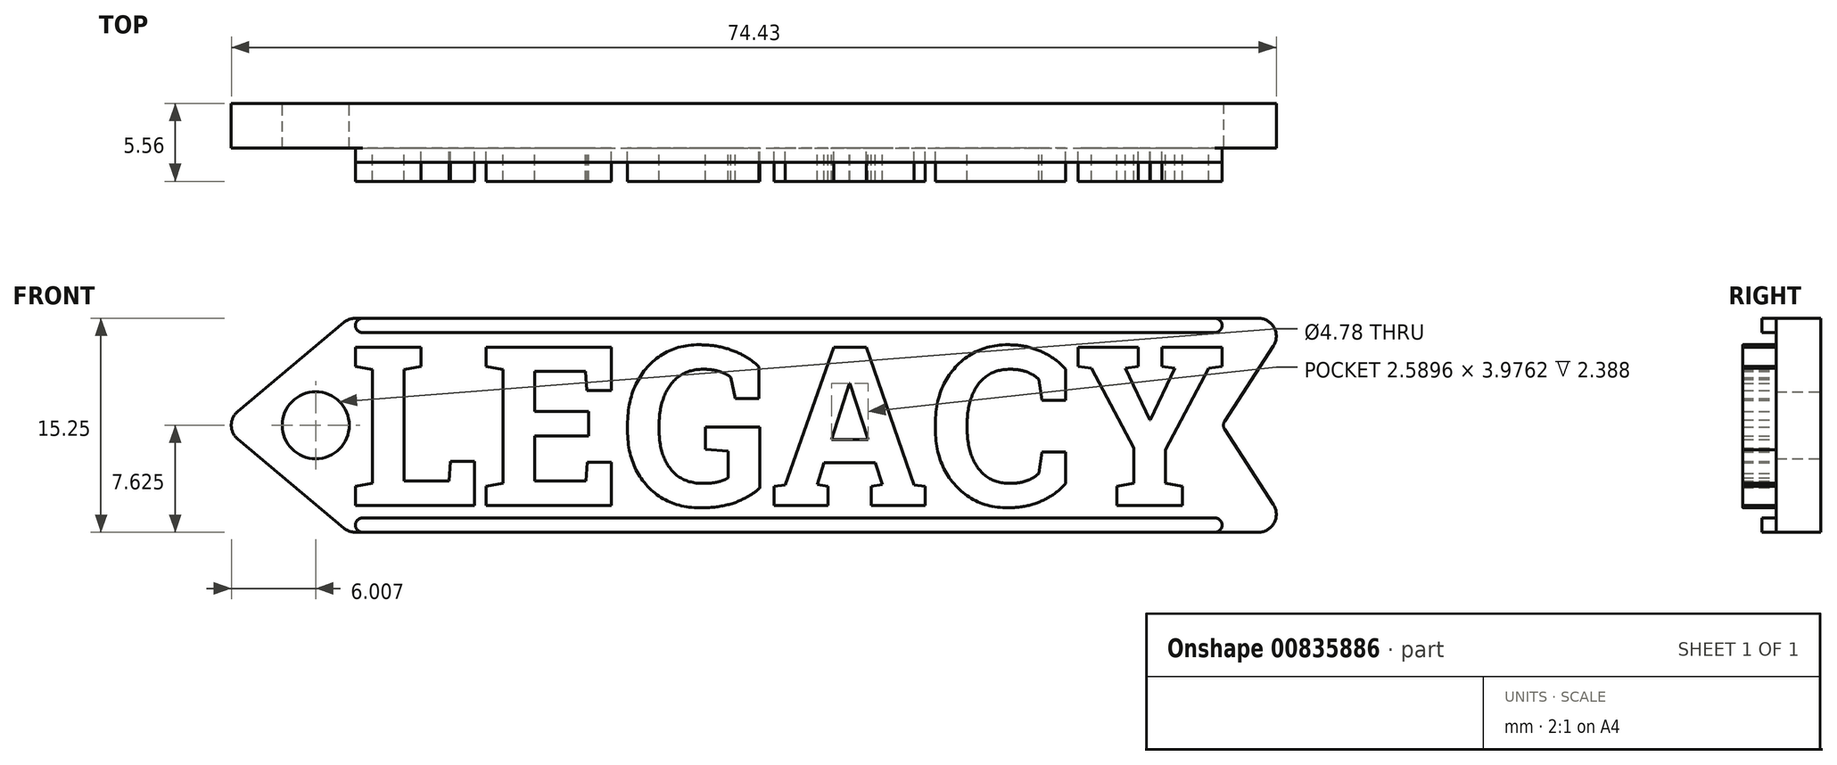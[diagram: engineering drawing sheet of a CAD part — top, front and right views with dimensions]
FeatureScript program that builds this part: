
annotation { "Feature Type Name" : "Feature", "Feature Type Description" : "" }
export const myFeature = defineFeature(function(context is Context, id is Id, definition is map)
    precondition{}
    {
        {
            var Q0;
            Q0=qCreatedBy(makeId("Front.planeOp"),FACE);
            var sketch = newSketch(context, id + "F0", { "sketchPlane" : qUnion([Q0])});
            skLineSegment(sketch, "E0.bottom", {"start": v(0, 0) * mm, "end": v(76.2, 0) * mm});
            skLineSegment(sketch, "E0.top", {"start": v(0, 19.05) * mm, "end": v(76.2, 19.05) * mm});
            skLineSegment(sketch, "E0.left", {"start": v(0, 0) * mm, "end": v(0, 19.05) * mm});
            skLineSegment(sketch, "E0.right", {"start": v(76.2, 0) * mm, "end": v(76.2, 19.05) * mm});
            skLineSegment(sketch, "E1", {"start": v(0, 9.53) * mm, "end": v(11.35, 19.05) * mm});
            skLineSegment(sketch, "E2", {"start": v(0, 9.53) * mm, "end": v(11.35, 0) * mm});
            skLineSegment(sketch, "E3", {"start": v(0, 9.53) * mm, "end": v(11.35, 9.53) * mm});
            skCircle(sketch, "E4", {"center": v(6.72, 9.53) * mm, "radius": 2.39 * mm});
            skText(sketch, "E5", { "text": "LEGACY", "fontName": "RobotoSlab-Bold.ttf"});
            skLineSegment(sketch, "E6", {"start": v(76.2, 19.05) * mm, "end": v(76.2, 15.24) * mm});
            skLineSegment(sketch, "E7", {"start": v(76.2, 0) * mm, "end": v(76.2, 3.81) * mm});
            skLineSegment(sketch, "E8", {"start": v(76.2, 1.9) * mm, "end": v(9.08, 1.9) * mm});
            skLineSegment(sketch, "E9", {"start": v(76.2, 17.15) * mm, "end": v(9.08, 17.15) * mm});
            const initialGuessF0  = {"E5": [0.01135, 0.00381, 1, 0, 0.01143]};
            skSetInitialGuess(sketch, initialGuessF0);
            skSolve(sketch);
        }
        {
            var Q0;
            {var subQ1=sQuery(id+"F0.wireOp",EDGE,"E0.right");Q0=makeQuery(id+"F0.imprint","IMPRINT",FACE,{"disambiguationData":[TD([[makeQuery(id+"F0.imprint","IMPRINT",EDGE,{"derivedFrom":subQ1}),1.0]])]});}
            var Q1;
            {var subQ0=sQuery(id+"F0.wireOp",EDGE,"E0.right");Q1=makeQuery(id+"F0.imprint","IMPRINT",FACE,{"disambiguationData":[TD([[makeQuery(id+"F0.imprint","IMPRINT",EDGE,{"derivedFrom":subQ0}),1.0]])]});}
            var Q2;
            Q2=makeQuery(id+"F0.imprint","IMPRINT",FACE,{"disambiguationData":[TD([[makeQuery(id+"F0.imprint","IMPRINT",EDGE,{"derivedFrom":sQuery(id+"F0.wireOp",EDGE,"E5.sketch_text.stroke-0")}),-1.0]])]});
            var Q3;
            Q3=makeQuery(id+"F0.imprint","IMPRINT",FACE,{"disambiguationData":[TD([[makeQuery(id+"F0.imprint","IMPRINT",EDGE,{"derivedFrom":sQuery(id+"F0.wireOp",EDGE,"E5.sketch_text.stroke-16")}),-1.0]])]});
            var Q4;
            Q4=makeQuery(id+"F0.imprint","IMPRINT",FACE,{"disambiguationData":[TD([[makeQuery(id+"F0.imprint","IMPRINT",EDGE,{"derivedFrom":sQuery(id+"F0.wireOp",EDGE,"E5.sketch_text.stroke-37")}),-1.0]])]});
            var Q5;
            Q5=makeQuery(id+"F0.imprint","IMPRINT",FACE,{"disambiguationData":[TD([[makeQuery(id+"F0.imprint","IMPRINT",EDGE,{"derivedFrom":sQuery(id+"F0.wireOp",EDGE,"E5.sketch_text.stroke-63")}),-1.0]])]});
            var Q6;
            Q6=makeQuery(id+"F0.imprint","IMPRINT",FACE,{"disambiguationData":[TD([[makeQuery(id+"F0.imprint","IMPRINT",EDGE,{"derivedFrom":sQuery(id+"F0.wireOp",EDGE,"E5.sketch_text.stroke-79")}),1.0]])]});
            var Q7;
            Q7=makeQuery(id+"F0.imprint","IMPRINT",FACE,{"disambiguationData":[TD([[makeQuery(id+"F0.imprint","IMPRINT",EDGE,{"derivedFrom":sQuery(id+"F0.wireOp",EDGE,"E5.sketch_text.stroke-83")}),-1.0]])]});
            var Q8;
            Q8=makeQuery(id+"F0.imprint","IMPRINT",FACE,{"disambiguationData":[TD([[makeQuery(id+"F0.imprint","IMPRINT",EDGE,{"derivedFrom":sQuery(id+"F0.wireOp",EDGE,"E5.sketch_text.stroke-107")}),-1.0]])]});
            extrude(context, id + "F1", {"entities" : qUnion([Q0, Q1, Q2, Q3, Q4, Q5, Q6, Q7, Q8]), "depth" : 3.17 * mm, "offsetDistance" : 25.4 * mm});
        }
        {
            var Q0;
            Q0=makeQuery(id+"F1.opExtrude","CAP_FACE",FACE,{"disambiguationData":[OSD([sQuery(id+"F0.wireOp",EDGE,"E0.right"),sQuery(id+"F0.wireOp",EDGE,"E1"),sQuery(id+"F0.wireOp",EDGE,"E2"),sQuery(id+"F0.wireOp",EDGE,"E6"),sQuery(id+"F0.wireOp",EDGE,"E7"),sQuery(id+"F0.wireOp",EDGE,"E8"),sQuery(id+"F0.wireOp",EDGE,"E9")])],"isStart":false});
            var sketch = newSketch(context, id + "F2", { "sketchPlane" : qUnion([Q0])});
            skLineSegment(sketch, "E10.bottom", {"start": v(0, 0) * mm, "end": v(76.2, 0) * mm});
            skLineSegment(sketch, "E10.top", {"start": v(0, 19.05) * mm, "end": v(76.2, 19.05) * mm});
            skLineSegment(sketch, "E10.left", {"start": v(0, 0) * mm, "end": v(0, 19.05) * mm});
            skLineSegment(sketch, "E10.right", {"start": v(76.2, 0) * mm, "end": v(76.2, 19.05) * mm});
            skText(sketch, "E11", { "text": "LEGACY", "fontName": "RobotoSlab-Bold.ttf"});
            skLineSegment(sketch, "E12", {"start": v(0, 9.53) * mm, "end": v(11.35, 19.05) * mm});
            skLineSegment(sketch, "E13", {"start": v(0, 9.53) * mm, "end": v(11.35, 0) * mm});
            const initialGuessF2  = {"E11": [0.00912, 0.00381, 1, 0, 0.01143]};
            skSetInitialGuess(sketch, initialGuessF2);
            skSolve(sketch);
        }
        {
            var Q0;
            Q0=makeQuery(id+"F2.imprint","IMPRINT",FACE,{"disambiguationData":[TD([[makeQuery(id+"F2.imprint","IMPRINT",EDGE,{"derivedFrom":sQuery(id+"F2.wireOp",EDGE,"E11.sketch_text.stroke-0")}),-1.0]])]});
            var Q1;
            Q1=makeQuery(id+"F2.imprint","IMPRINT",FACE,{"disambiguationData":[TD([[makeQuery(id+"F2.imprint","IMPRINT",EDGE,{"derivedFrom":sQuery(id+"F2.wireOp",EDGE,"E11.sketch_text.stroke-16")}),-1.0]])]});
            var Q2;
            Q2=makeQuery(id+"F2.imprint","IMPRINT",FACE,{"disambiguationData":[TD([[makeQuery(id+"F2.imprint","IMPRINT",EDGE,{"derivedFrom":sQuery(id+"F2.wireOp",EDGE,"E11.sketch_text.stroke-37")}),-1.0]])]});
            var Q3;
            Q3=makeQuery(id+"F2.imprint","IMPRINT",FACE,{"disambiguationData":[TD([[makeQuery(id+"F2.imprint","IMPRINT",EDGE,{"derivedFrom":sQuery(id+"F2.wireOp",EDGE,"E11.sketch_text.stroke-63")}),-1.0]])]});
            var Q4;
            Q4=makeQuery(id+"F2.imprint","IMPRINT",FACE,{"disambiguationData":[TD([[makeQuery(id+"F2.imprint","IMPRINT",EDGE,{"derivedFrom":sQuery(id+"F2.wireOp",EDGE,"E11.sketch_text.stroke-83")}),-1.0]])]});
            var Q5;
            Q5=makeQuery(id+"F2.imprint","IMPRINT",FACE,{"disambiguationData":[TD([[makeQuery(id+"F2.imprint","IMPRINT",EDGE,{"derivedFrom":sQuery(id+"F2.wireOp",EDGE,"E11.sketch_text.stroke-107")}),-1.0]])]});
            extrude(context, id + "F3", {"entities" : qUnion([Q0, Q1, Q2, Q3, Q4, Q5]), "operationType" : NewBodyOperationType.ADD, "depth" : 2.4 * mm, "offsetDistance" : 25.4 * mm});
        }
        {
            var Q0;
            {var subQ0=sQuery(id+"F0.wireOp",EDGE,"E7");var subQ1=sQuery(id+"F0.wireOp",EDGE,"E6");var subQ2=sQuery(id+"F0.wireOp",EDGE,"E0.right");var subQ3=sQuery(id+"F0.wireOp",EDGE,"E2");var subQ4=sQuery(id+"F0.wireOp",EDGE,"E4");var subQ5=sQuery(id+"F0.wireOp",EDGE,"E8");var subQ6=sQuery(id+"F0.wireOp",EDGE,"E9");var subQ7=sQuery(id+"F0.wireOp",EDGE,"E1");Q0=makeQuery(id+"F3.boolean.opBoolean","SPLIT",FACE,{"disambiguationData":[TD([makeQuery(id+"F1.opExtrude","SWEPT_FACE",FACE,{"disambiguationData":[OSD([subQ4])]})])],"derivedFrom":makeQuery(id+"F1.opExtrude","CAP_FACE",FACE,{"disambiguationData":[OSD([subQ4,subQ2,subQ7,subQ3,subQ1,subQ0,subQ5,subQ6])],"isStart":false})});}
            var sketch = newSketch(context, id + "F4", { "sketchPlane" : qUnion([Q0])});
            skLineSegment(sketch, "E14", {"start": v(71.27, 9.53) * mm, "end": v(76.2, 17.15) * mm});
            skLineSegment(sketch, "E15", {"start": v(71.27, 9.53) * mm, "end": v(76.2, 1.9) * mm});
            skSolve(sketch);
        }
        {
            var Q0;
            Q0=makeQuery(id+"F4.imprint","IMPRINT",FACE,{"disambiguationData":[TD([[makeQuery(id+"F4.imprint","IMPRINT",EDGE,{"derivedFrom":sQuery(id+"F4.wireOp",EDGE,"E14")}),-1.0]])]});
            extrude(context, id + "F5", {"entities" : qUnion([Q0]), "operationType" : NewBodyOperationType.REMOVE, "oppositeDirection" : true, "depth" : 25.4 * mm, "offsetDistance" : 25.4 * mm});
        }
        {
            var Q0;
            Q0=makeQuery(id+"F1.opExtrude","SWEPT_EDGE",EDGE,{"disambiguationData":[OSD([sQuery(id+"F0.wireOp",EDGE,"E0.left"),sQuery(id+"F0.wireOp",EDGE,"E1"),sQuery(id+"F0.wireOp",EDGE,"E2")])]});
            var Q1;
            Q1=makeQuery(id+"F1.opExtrude","SWEPT_EDGE",EDGE,{"disambiguationData":[OSD([sQuery(id+"F0.wireOp",EDGE,"E1"),sQuery(id+"F0.wireOp",EDGE,"E9")])]});
            var Q2;
            Q2=makeQuery(id+"F1.opExtrude","SWEPT_EDGE",EDGE,{"disambiguationData":[OSD([sQuery(id+"F0.wireOp",EDGE,"E2"),sQuery(id+"F0.wireOp",EDGE,"E8")])]});
            fillet(context, id + "F6", {"entities" : qUnion([Q0, Q1, Q2]), "radius" : 1.27 * mm, "tangentPropagation" : true, "allowEdgeOverflow" : false});
        }
        {
            var Q0;
            {var subQ0=sQuery(id+"F0.wireOp",EDGE,"E9");var subQ1=sQuery(id+"F0.wireOp",EDGE,"E6");Q0=makeQuery(id+"F5.boolean.opBoolean","MERGE",EDGE,{"derivedFrom":[makeQuery(id+"F1.opExtrude","SWEPT_EDGE",EDGE,{"disambiguationData":[OSD([subQ1,subQ0])]}),makeQuery(id+"F5.opExtrude","SWEPT_EDGE",EDGE,{"disambiguationData":[OSD([sQuery(id+"F0.wireOp",EDGE,"E0.right"),subQ1,sQuery(id+"F0.wireOp",EDGE,"E7"),subQ0,sQuery(id+"F4.wireOp",EDGE,"E14")])]})]});}
            var Q1;
            {var subQ0=sQuery(id+"F0.wireOp",EDGE,"E8");var subQ1=sQuery(id+"F0.wireOp",EDGE,"E7");Q1=makeQuery(id+"F5.boolean.opBoolean","MERGE",EDGE,{"derivedFrom":[makeQuery(id+"F1.opExtrude","SWEPT_EDGE",EDGE,{"disambiguationData":[OSD([subQ1,subQ0])]}),makeQuery(id+"F5.opExtrude","SWEPT_EDGE",EDGE,{"disambiguationData":[OSD([sQuery(id+"F0.wireOp",EDGE,"E0.right"),sQuery(id+"F0.wireOp",EDGE,"E6"),subQ1,subQ0,sQuery(id+"F4.wireOp",EDGE,"E15")])]})]});}
            var Q2;
            Q2=makeQuery(id+"F5.boolean.opBoolean","COPY",EDGE,{"derivedFrom":makeQuery(id+"F5.opExtrude","SWEPT_EDGE",EDGE,{"disambiguationData":[OSD([sQuery(id+"F4.wireOp",EDGE,"E14"),sQuery(id+"F4.wireOp",EDGE,"E15")])]})});
            fillet(context, id + "F7", {"entities" : qUnion([Q0, Q1, Q2]), "radius" : 0.5 * mm, "tangentPropagation" : true, "allowEdgeOverflow" : false});
        }
        {
            var Q0;
            {var subQ0=sQuery(id+"F0.wireOp",EDGE,"E7");var subQ1=sQuery(id+"F0.wireOp",EDGE,"E6");var subQ2=sQuery(id+"F0.wireOp",EDGE,"E0.right");var subQ3=sQuery(id+"F0.wireOp",EDGE,"E2");var subQ4=sQuery(id+"F0.wireOp",EDGE,"E4");var subQ5=sQuery(id+"F0.wireOp",EDGE,"E8");var subQ6=sQuery(id+"F0.wireOp",EDGE,"E9");var subQ7=sQuery(id+"F0.wireOp",EDGE,"E1");Q0=makeQuery(id+"F3.boolean.opBoolean","SPLIT",FACE,{"disambiguationData":[TD([makeQuery(id+"F1.opExtrude","SWEPT_FACE",FACE,{"disambiguationData":[OSD([subQ4])]})])],"derivedFrom":makeQuery(id+"F1.opExtrude","CAP_FACE",FACE,{"disambiguationData":[OSD([subQ4,subQ2,subQ7,subQ3,subQ1,subQ0,subQ5,subQ6])],"isStart":false})});}
            var sketch = newSketch(context, id + "F8", { "sketchPlane" : qUnion([Q0])});
            skLineSegment(sketch, "E16", {"start": v(9.54, 17.15) * mm, "end": v(9.54, 16.13) * mm});
            skLineSegment(sketch, "E17", {"start": v(9.54, 1.9) * mm, "end": v(9.54, 2.92) * mm});
            skLineSegment(sketch, "E18", {"start": v(9.54, 16.13) * mm, "end": v(71.27, 16.13) * mm});
            skLineSegment(sketch, "E19", {"start": v(71.27, 16.13) * mm, "end": v(71.27, 17.15) * mm});
            skLineSegment(sketch, "E20", {"start": v(9.54, 2.92) * mm, "end": v(71.27, 2.92) * mm});
            skLineSegment(sketch, "E21", {"start": v(71.27, 2.92) * mm, "end": v(71.27, 1.9) * mm});
            skSolve(sketch);
        }
        {
            var Q0;
            Q0=makeQuery(id+"F8.imprint","IMPRINT",FACE,{"disambiguationData":[TD([[makeQuery(id+"F8.imprint","IMPRINT",EDGE,{"derivedFrom":sQuery(id+"F8.wireOp",EDGE,"E16")}),1.0]])]});
            var Q1;
            Q1=makeQuery(id+"F8.imprint","IMPRINT",FACE,{"disambiguationData":[TD([[makeQuery(id+"F8.imprint","IMPRINT",EDGE,{"derivedFrom":sQuery(id+"F8.wireOp",EDGE,"E17")}),-1.0]])]});
            extrude(context, id + "F9", {"entities" : qUnion([Q0, Q1]), "operationType" : NewBodyOperationType.ADD, "depth" : 1.02 * mm, "offsetDistance" : 25.4 * mm});
        }
        {
            var Q0;
            Q0=makeQuery(id+"F9.opExtrude","SWEPT_EDGE",EDGE,{"disambiguationData":[OSD([sQuery(id+"F8.wireOp",EDGE,"E17"),sQuery(id+"F8.wireOp",EDGE,"lsGSmF26-6XCD-bxu5-NAPA-QOUgoa4W5BEv")])]});
            var Q1;
            Q1=makeQuery(id+"F9.opExtrude","SWEPT_EDGE",EDGE,{"disambiguationData":[OSD([sQuery(id+"F0.wireOp",EDGE,"E4"),sQuery(id+"F0.wireOp",EDGE,"E0.right"),sQuery(id+"F0.wireOp",EDGE,"E1"),sQuery(id+"F0.wireOp",EDGE,"E2"),sQuery(id+"F0.wireOp",EDGE,"E6"),sQuery(id+"F0.wireOp",EDGE,"E7"),sQuery(id+"F0.wireOp",EDGE,"E8"),sQuery(id+"F0.wireOp",EDGE,"E9"),sQuery(id+"F8.wireOp",EDGE,"E17")])]});
            var Q2;
            Q2=makeQuery(id+"F9.opExtrude","SWEPT_EDGE",EDGE,{"disambiguationData":[OSD([sQuery(id+"F0.wireOp",EDGE,"E4"),sQuery(id+"F0.wireOp",EDGE,"E0.right"),sQuery(id+"F0.wireOp",EDGE,"E1"),sQuery(id+"F0.wireOp",EDGE,"E2"),sQuery(id+"F0.wireOp",EDGE,"E6"),sQuery(id+"F0.wireOp",EDGE,"E7"),sQuery(id+"F0.wireOp",EDGE,"E8"),sQuery(id+"F0.wireOp",EDGE,"E9"),sQuery(id+"F4.wireOp",EDGE,"E15"),sQuery(id+"F8.wireOp",EDGE,"WcreGEJM-yhBB-p1cp-J6fE-w1TStOfON3k8")])]});
            var Q3;
            Q3=makeQuery(id+"F9.opExtrude","SWEPT_EDGE",EDGE,{"disambiguationData":[OSD([sQuery(id+"F8.wireOp",EDGE,"lsGSmF26-6XCD-bxu5-NAPA-QOUgoa4W5BEv"),sQuery(id+"F8.wireOp",EDGE,"WcreGEJM-yhBB-p1cp-J6fE-w1TStOfON3k8")])]});
            var Q4;
            Q4=makeQuery(id+"F9.opExtrude","SWEPT_EDGE",EDGE,{"disambiguationData":[OSD([sQuery(id+"F8.wireOp",EDGE,"wXEXPmjd-5oel-4P8e-rDGC-djeAD9JOo1a8"),sQuery(id+"F8.wireOp",EDGE,"jKHDVzED-92ZQ-R1I0-7juc-dkRHElyn2IOm")])]});
            var Q5;
            Q5=makeQuery(id+"F9.opExtrude","SWEPT_EDGE",EDGE,{"disambiguationData":[OSD([sQuery(id+"F0.wireOp",EDGE,"E4"),sQuery(id+"F0.wireOp",EDGE,"E0.right"),sQuery(id+"F0.wireOp",EDGE,"E1"),sQuery(id+"F0.wireOp",EDGE,"E2"),sQuery(id+"F0.wireOp",EDGE,"E6"),sQuery(id+"F0.wireOp",EDGE,"E7"),sQuery(id+"F0.wireOp",EDGE,"E8"),sQuery(id+"F0.wireOp",EDGE,"E9"),sQuery(id+"F4.wireOp",EDGE,"E14"),sQuery(id+"F8.wireOp",EDGE,"jKHDVzED-92ZQ-R1I0-7juc-dkRHElyn2IOm")])]});
            var Q6;
            Q6=makeQuery(id+"F9.opExtrude","SWEPT_EDGE",EDGE,{"disambiguationData":[OSD([sQuery(id+"F0.wireOp",EDGE,"E4"),sQuery(id+"F0.wireOp",EDGE,"E0.right"),sQuery(id+"F0.wireOp",EDGE,"E1"),sQuery(id+"F0.wireOp",EDGE,"E2"),sQuery(id+"F0.wireOp",EDGE,"E6"),sQuery(id+"F0.wireOp",EDGE,"E7"),sQuery(id+"F0.wireOp",EDGE,"E8"),sQuery(id+"F0.wireOp",EDGE,"E9"),sQuery(id+"F8.wireOp",EDGE,"E16")])]});
            var Q7;
            Q7=makeQuery(id+"F9.opExtrude","SWEPT_EDGE",EDGE,{"disambiguationData":[OSD([sQuery(id+"F8.wireOp",EDGE,"E16"),sQuery(id+"F8.wireOp",EDGE,"wXEXPmjd-5oel-4P8e-rDGC-djeAD9JOo1a8")])]});
            var Q8;
            Q8=makeQuery(id+"F9.opExtrude","SWEPT_EDGE",EDGE,{"disambiguationData":[OSD([sQuery(id+"F8.wireOp",EDGE,"E20"),sQuery(id+"F8.wireOp",EDGE,"E21")])]});
            var Q9;
            Q9=makeQuery(id+"F9.opExtrude","SWEPT_EDGE",EDGE,{"disambiguationData":[OSD([sQuery(id+"F0.wireOp",EDGE,"E8"),sQuery(id+"F8.wireOp",EDGE,"E21")])]});
            var Q10;
            Q10=makeQuery(id+"F9.opExtrude","SWEPT_EDGE",EDGE,{"disambiguationData":[OSD([sQuery(id+"F0.wireOp",EDGE,"E9"),sQuery(id+"F8.wireOp",EDGE,"E19")])]});
            var Q11;
            Q11=makeQuery(id+"F9.opExtrude","SWEPT_EDGE",EDGE,{"disambiguationData":[OSD([sQuery(id+"F8.wireOp",EDGE,"E18"),sQuery(id+"F8.wireOp",EDGE,"E19")])]});
            fillet(context, id + "F10", {"entities" : qUnion([Q0, Q1, Q2, Q3, Q4, Q5, Q6, Q7, Q8, Q9, Q10, Q11]), "radius" : 0.5 * mm, "tangentPropagation" : true, "allowEdgeOverflow" : false});
        }
    });
